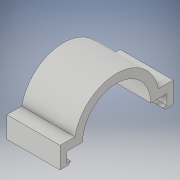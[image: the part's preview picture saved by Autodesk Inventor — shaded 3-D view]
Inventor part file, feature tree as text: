
AUTODESK INVENTOR PART (.ipt)
format: ipt  version: 2018 (Build 220112000, 112)  size: 122,880 bytes
history: native  units: in
note: dims shown in document units (in); Inventor stores cm internally (conversion verified against a paired STEP export)
features: extrude x1, sketch x1
ambient origin geometry x8: Origin, YZ Plane, XZ Plane, XY Plane, X Axis, Y Axis, Z Axis, Center Point
bodies: Solid1 (feature_tree)
feature tree (2):
  extrude  "Extrusion1"  Depth=0.2in
  sketch  "Sketch1"  dims[d0=1.6in d1=2.0in d3=0.24in d4=0.1in d5=135.0deg d6=0.2in d7=0.0in d8=0.35in d9=0.5in d10=1.25in d11=0.0in d12=0.2in]
